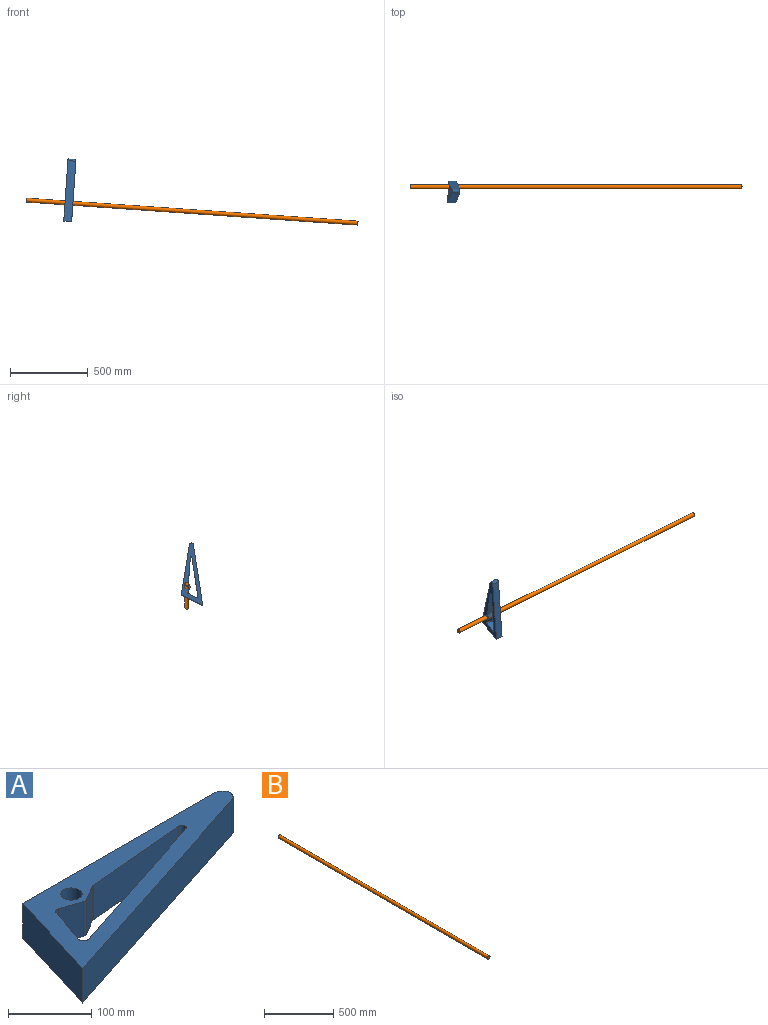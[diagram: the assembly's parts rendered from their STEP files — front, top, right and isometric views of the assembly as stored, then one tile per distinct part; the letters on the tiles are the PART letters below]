
ASSEMBLY  parts=2 mates=1
PART A: 17 faces, bbox 383.1x145.7x50.8 mm
  f0: plane 374.27x120.96mm, normal (0.31,-0.95,0), area 19981.1mm2, adj f1,f14,f15,f16
  f1: cylinder r=12.7mm len=50.8mm, axis (0,0,-1), area 1825.2mm2, adj f0,f2,f15,f16
  f2: plane 325.81x50.8mm, normal (0,1,0), area 16550.9mm2, adj f1,f14,f15,f16
  f3: cylinder r=6.35mm len=50.8mm, axis (0,0,-1), area 711.7mm2, adj f4,f13,f15,f16
  f4: plane 57.7x50.8mm, normal (0.95,-0.32,0), area 3090.8mm2, adj f3,f5,f15,f16
  f5: cylinder r=6.35mm len=50.8mm, axis (0,0,-1), area 506.7mm2, adj f4,f6,f15,f16
  f6: plane 50.8x31.96mm, normal (-0.32,-0.95,0), area 1712.3mm2, adj f5,f7,f15,f16
  f7: cylinder r=6.35mm len=50.8mm, axis (0,0,-1), area 277.6mm2, adj f6,f8,f15,f16
  f8: plane 50.8x24.32mm, normal (0.51,-0.86,0), area 1438.2mm2, adj f7,f9,f15,f16
  f9: cylinder r=6.35mm len=50.8mm, axis (0,0,-1), area 145.2mm2, adj f8,f10,f15,f16
  f10: plane 159.06x50.8mm, normal (0.09,-1,0), area 8111.4mm2, adj f9,f11,f15,f16
  f11: cylinder r=5.08mm len=50.8mm, axis (0,0,-1), area 752.7mm2, adj f10,f13,f15,f16
  f12: cylinder r=12.74mm len=50.8mm, axis (0,0,-1), area 4065.8mm2, adj f15,f16
  f13: plane 244.68x79.08mm, normal (-0.31,0.95,0), area 13062.9mm2, adj f3,f11,f15,f16
  f14: plane 145.74x50.8mm, normal (-0.96,0.29,0), area 7741.9mm2, adj f0,f2,f15,f16
  f15: plane 383.06x145.74mm, normal (0,0,1), area 19277.6mm2, adj f0,f1,f2,f3,f4,f5,f6,f7
  f16: plane 383.06x145.74mm, normal (0,0,-1), area 19277.6mm2, adj f0,f1,f2,f3,f4,f5,f6,f7
PART B: 3 faces, bbox 25.4x2133.6x25.4 mm
  f0: cylinder r=12.7mm len=2133.6mm, axis (0,1,0), area 170253.7mm2, adj f1,f2
  f1: plane 25.4x25.4mm, normal (0,-1,0), area 506.7mm2, adj f0
  f2: plane 25.4x25.4mm, normal (0,1,0), area 506.7mm2, adj f0
PLACE A rot(axis=(0.08,-0.99,-0.09),86.4deg) t=(-43.14,-5.99,86.15)mm
PLACE B rot(axis=(-0.55,0.59,0.59),122.3deg) t=(-354.27,57.27,-51.51)mm
MATE cylindrical B.f0 <-> A.f12  axis (-1,0,0.07) through (-354.27,57.27,-51.51)mm
